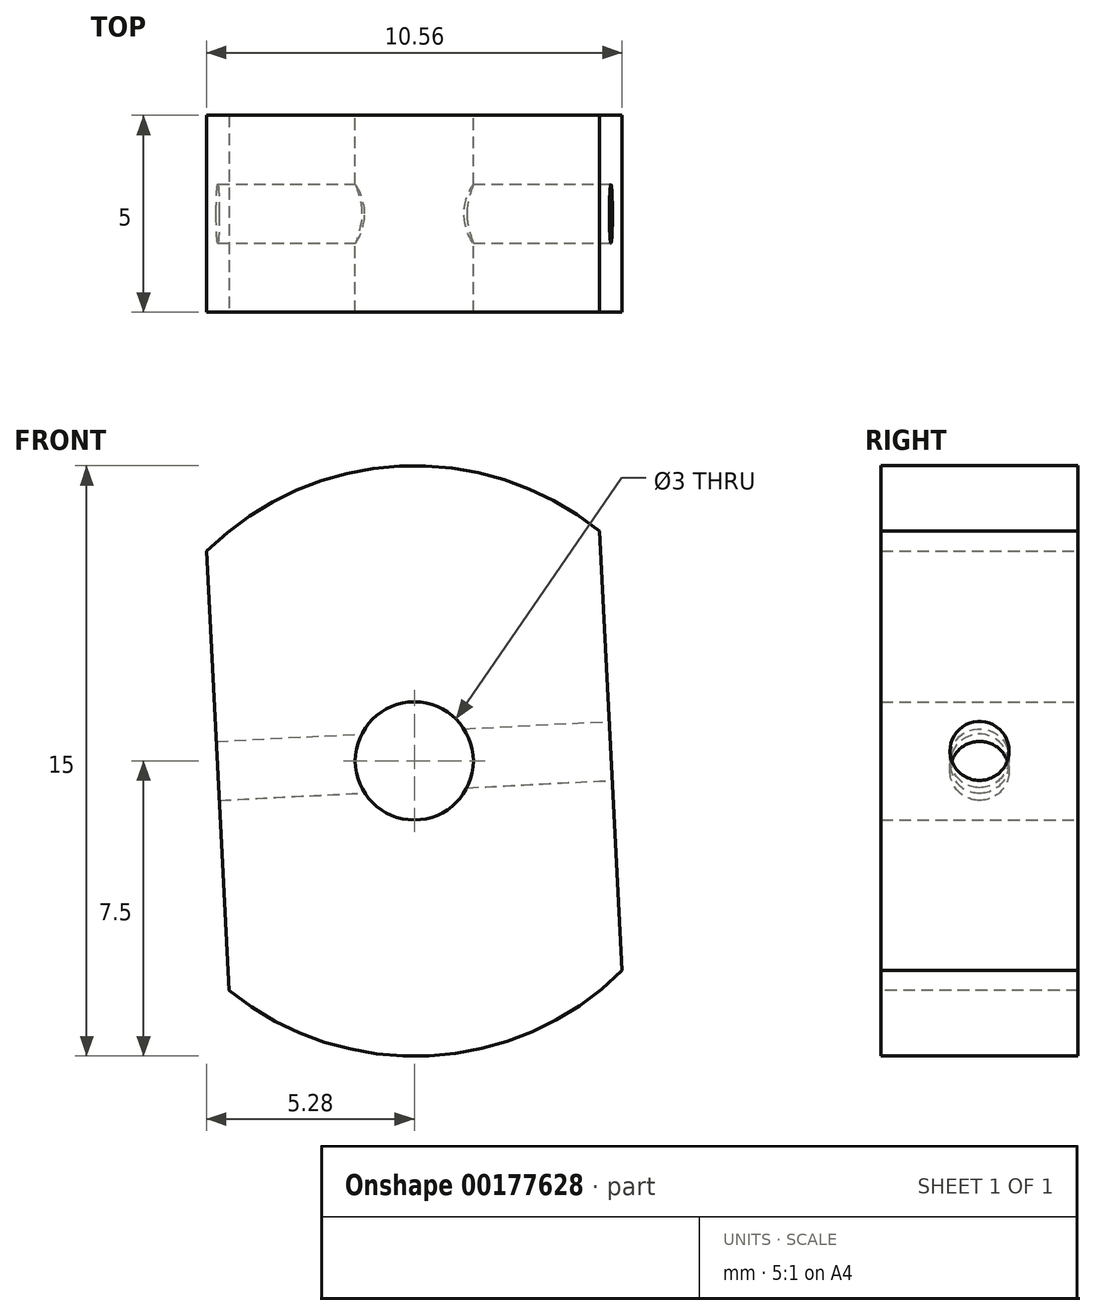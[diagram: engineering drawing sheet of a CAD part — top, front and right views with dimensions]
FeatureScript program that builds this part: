
annotation { "Feature Type Name" : "Feature", "Feature Type Description" : "" }
export const myFeature = defineFeature(function(context is Context, id is Id, definition is map)
    precondition{}
    {
        {
            var Q0;
            Q0=qCreatedBy(makeId("Front.planeOp"),FACE);
            var sketch = newSketch(context, id + "F0", { "sketchPlane" : qUnion([Q0])});
            skCircle(sketch, "E0", {"center": v(0, 0) * mm, "radius": 7.5 * mm});
            skCircle(sketch, "E1", {"center": v(0, 0) * mm, "radius": 1.5 * mm});
            skSolve(sketch);
        }
        {
            var Q0;
            Q0=qSketchRegion(id+"F0",true);
            extrude(context, id + "F1", {"entities" : qUnion([Q0]), "depth" : 5 * mm});
        }
        {
            var Q0;
            Q0=makeQuery(id+"F1.opExtrude","CAP_FACE",FACE,{"disambiguationData":[OSD([sQuery(id+"F0.wireOp",EDGE,"E0"),sQuery(id+"F0.wireOp",EDGE,"E1")])],"isStart":false});
            var sketch = newSketch(context, id + "F2", { "sketchPlane" : qUnion([Q0])});
            skLineSegment(sketch, "E2.left", {"start": v(4.71, 5.84) * mm, "end": v(5.34, -6.62) * mm});
            skLineSegment(sketch, "E2.right", {"start": v(-5.34, 6.62) * mm, "end": v(-4.71, -5.84) * mm});
            skPoint(sketch, "E2.middle", {"position": v(0, 0) * mm});
            skLineSegment(sketch, "E3", {"start": v(-5.34, 6.62) * mm, "end": v(-10.33, 6.97) * mm});
            skLineSegment(sketch, "E4", {"start": v(-10.33, 6.97) * mm, "end": v(-9.52, -9.1) * mm});
            skLineSegment(sketch, "E5", {"start": v(-9.52, -9.1) * mm, "end": v(-4.71, -5.84) * mm});
            skLineSegment(sketch, "E6", {"start": v(5.34, -6.62) * mm, "end": v(8.8, -9.1) * mm});
            skLineSegment(sketch, "E7", {"start": v(8.8, -9.1) * mm, "end": v(11.45, 0) * mm});
            skLineSegment(sketch, "E8", {"start": v(11.45, 0) * mm, "end": v(7.7, 6.24) * mm});
            skLineSegment(sketch, "E9", {"start": v(7.7, 6.24) * mm, "end": v(4.71, 5.84) * mm});
            skSolve(sketch);
        }
        {
            var Q0;
            Q0=qSketchRegion(id+"F2",true);
            extrude(context, id + "F3", {"entities" : qUnion([Q0]), "operationType" : NewBodyOperationType.REMOVE, "oppositeDirection" : true, "depth" : 25 * mm});
        }
        {
            var Q0;
            Q0=makeQuery(id+"F3.boolean.opBoolean","COPY",FACE,{"derivedFrom":makeQuery(id+"F3.opExtrude","SWEPT_FACE",FACE,{"disambiguationData":[OSD([sQuery(id+"F2.wireOp",EDGE,"E2.left")])]})});
            var sketch = newSketch(context, id + "F4", { "sketchPlane" : qUnion([Q0])});
            skCircle(sketch, "E10", {"center": v(-2.5, 0) * mm, "radius": 0.75 * mm});
            skSolve(sketch);
        }
        {
            var Q0;
            Q0=qSketchRegion(id+"F4",true);
            extrude(context, id + "F5", {"entities" : qUnion([Q0]), "operationType" : NewBodyOperationType.REMOVE, "oppositeDirection" : true, "depth" : 25 * mm});
        }
    });
